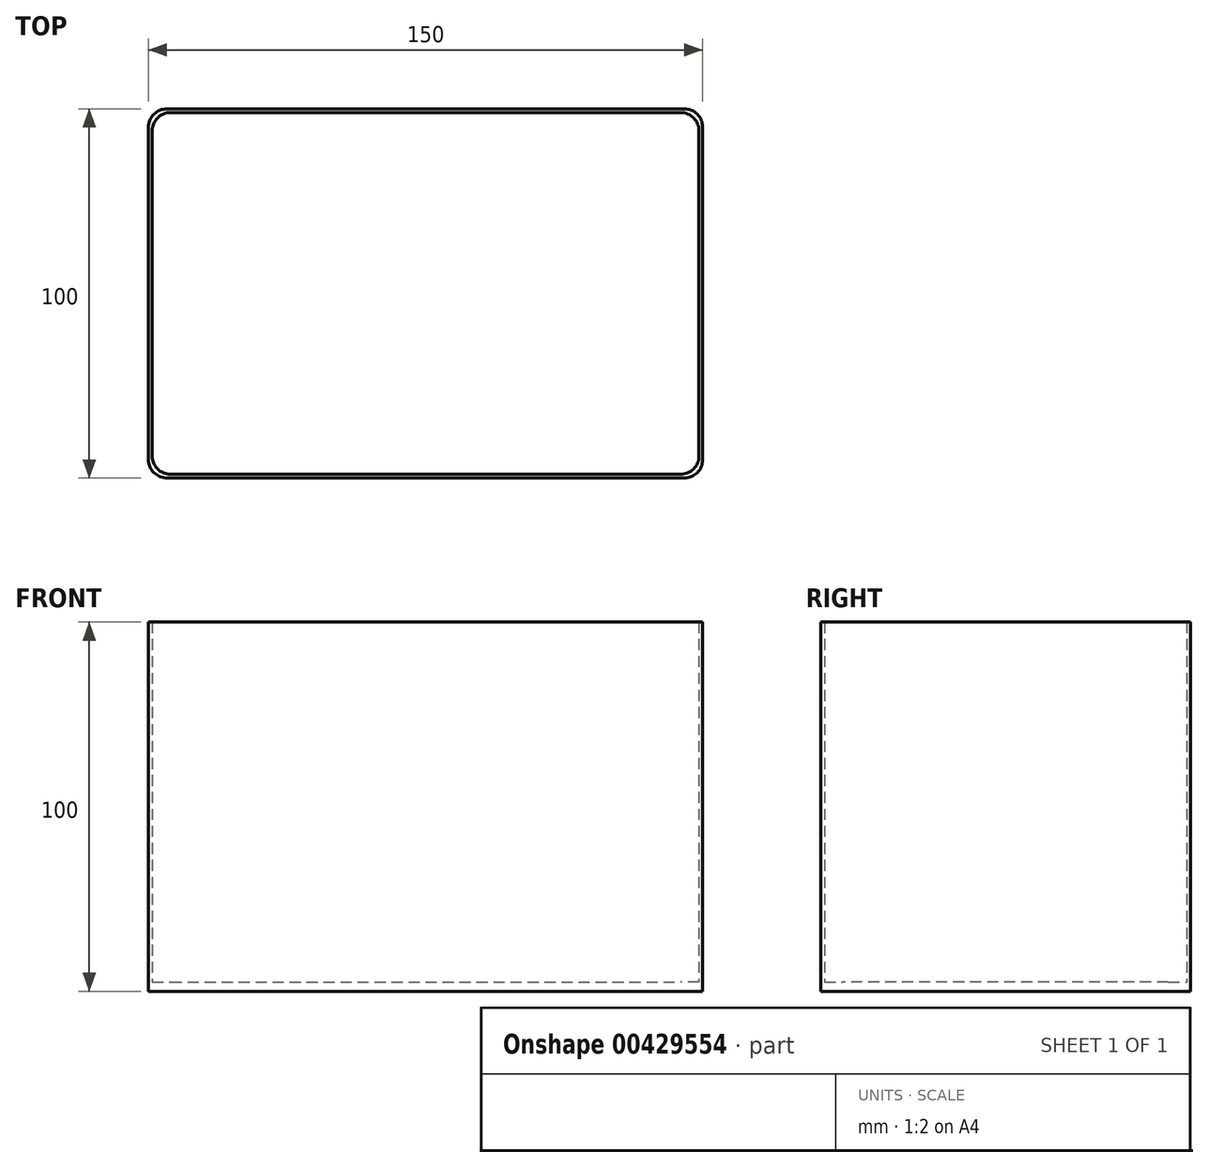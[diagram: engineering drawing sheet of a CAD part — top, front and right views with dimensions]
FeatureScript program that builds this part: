
annotation { "Feature Type Name" : "Feature", "Feature Type Description" : "" }
export const myFeature = defineFeature(function(context is Context, id is Id, definition is map)
    precondition{}
    {
        {
            var Q0;
            Q0=qCreatedBy(makeId("Top.planeOp"),FACE);
            var sketch = newSketch(context, id + "F0", { "sketchPlane" : qUnion([Q0])});
            skLineSegment(sketch, "E0.bottom", {"start": v(-68.7, 49.69) * mm, "end": v(71.3, 49.69) * mm});
            skLineSegment(sketch, "E0.top", {"start": v(-68.7, -50.31) * mm, "end": v(71.3, -50.31) * mm});
            skLineSegment(sketch, "E0.left", {"start": v(-73.7, 44.69) * mm, "end": v(-73.7, -45.31) * mm});
            skLineSegment(sketch, "E0.right", {"start": v(76.3, 44.69) * mm, "end": v(76.3, -45.31) * mm});
            skLineSegment(sketch, "E1.bottom", {"start": v(-67.7, 48.69) * mm, "end": v(70.3, 48.69) * mm});
            skLineSegment(sketch, "E1.top", {"start": v(-67.7, -49.31) * mm, "end": v(70.3, -49.31) * mm});
            skLineSegment(sketch, "E1.left", {"start": v(-72.7, 43.69) * mm, "end": v(-72.7, -44.31) * mm});
            skLineSegment(sketch, "E1.right", {"start": v(75.3, 43.69) * mm, "end": v(75.3, -44.31) * mm});
            skPoint(sketch, "E2.visualSharp", {"position": v(76.3, 49.69) * mm});
            skArc(sketch, "E2.filletArc", {"start": v(76.3, 44.69) * mm, "mid": v(74.84, 48.22) * mm, "end": v(71.3, 49.69) * mm});
            skPoint(sketch, "E3.visualSharp", {"position": v(75.3, 48.69) * mm});
            skArc(sketch, "E3.filletArc", {"start": v(75.3, 43.69) * mm, "mid": v(73.84, 47.22) * mm, "end": v(70.3, 48.69) * mm});
            skPoint(sketch, "E4.visualSharp", {"position": v(76.3, -50.31) * mm});
            skArc(sketch, "E4.filletArc", {"start": v(71.3, -50.31) * mm, "mid": v(74.84, -48.85) * mm, "end": v(76.3, -45.31) * mm});
            skPoint(sketch, "E5.visualSharp", {"position": v(75.3, -49.31) * mm});
            skArc(sketch, "E5.filletArc", {"start": v(70.3, -49.31) * mm, "mid": v(73.84, -47.85) * mm, "end": v(75.3, -44.31) * mm});
            skPoint(sketch, "E6.visualSharp", {"position": v(-73.7, 49.69) * mm});
            skArc(sketch, "E6.filletArc", {"start": v(-68.7, 49.69) * mm, "mid": v(-72.23, 48.22) * mm, "end": v(-73.7, 44.69) * mm});
            skPoint(sketch, "E7.visualSharp", {"position": v(-72.7, 48.69) * mm});
            skArc(sketch, "E7.filletArc", {"start": v(-67.7, 48.69) * mm, "mid": v(-71.23, 47.22) * mm, "end": v(-72.7, 43.69) * mm});
            skPoint(sketch, "E8.visualSharp", {"position": v(-73.7, -50.31) * mm});
            skArc(sketch, "E8.filletArc", {"start": v(-73.7, -45.31) * mm, "mid": v(-72.23, -48.85) * mm, "end": v(-68.7, -50.31) * mm});
            skPoint(sketch, "E9.visualSharp", {"position": v(-72.7, -49.31) * mm});
            skArc(sketch, "E9.filletArc", {"start": v(-72.7, -44.31) * mm, "mid": v(-71.23, -47.85) * mm, "end": v(-67.7, -49.31) * mm});
            skSolve(sketch);
        }
        {
            var Q0;
            Q0=makeQuery(id+"F0.imprint","IMPRINT",FACE,{"disambiguationData":[TD([[makeQuery(id+"F0.imprint","IMPRINT",EDGE,{"derivedFrom":sQuery(id+"F0.wireOp",EDGE,"E0.bottom")}),-1.0]])]});
            extrude(context, id + "F1", {"entities" : qUnion([Q0]), "depth" : 100 * mm});
        }
        {
            var Q0;
            Q0=makeQuery(id+"F0.imprint","IMPRINT",FACE,{"disambiguationData":[TD([[makeQuery(id+"F0.imprint","IMPRINT",EDGE,{"derivedFrom":sQuery(id+"F0.wireOp",EDGE,"E1.bottom")}),-1.0]])]});
            extrude(context, id + "F2", {"entities" : qUnion([Q0]), "operationType" : NewBodyOperationType.ADD, "depth" : 2.5 * mm});
        }
    });
